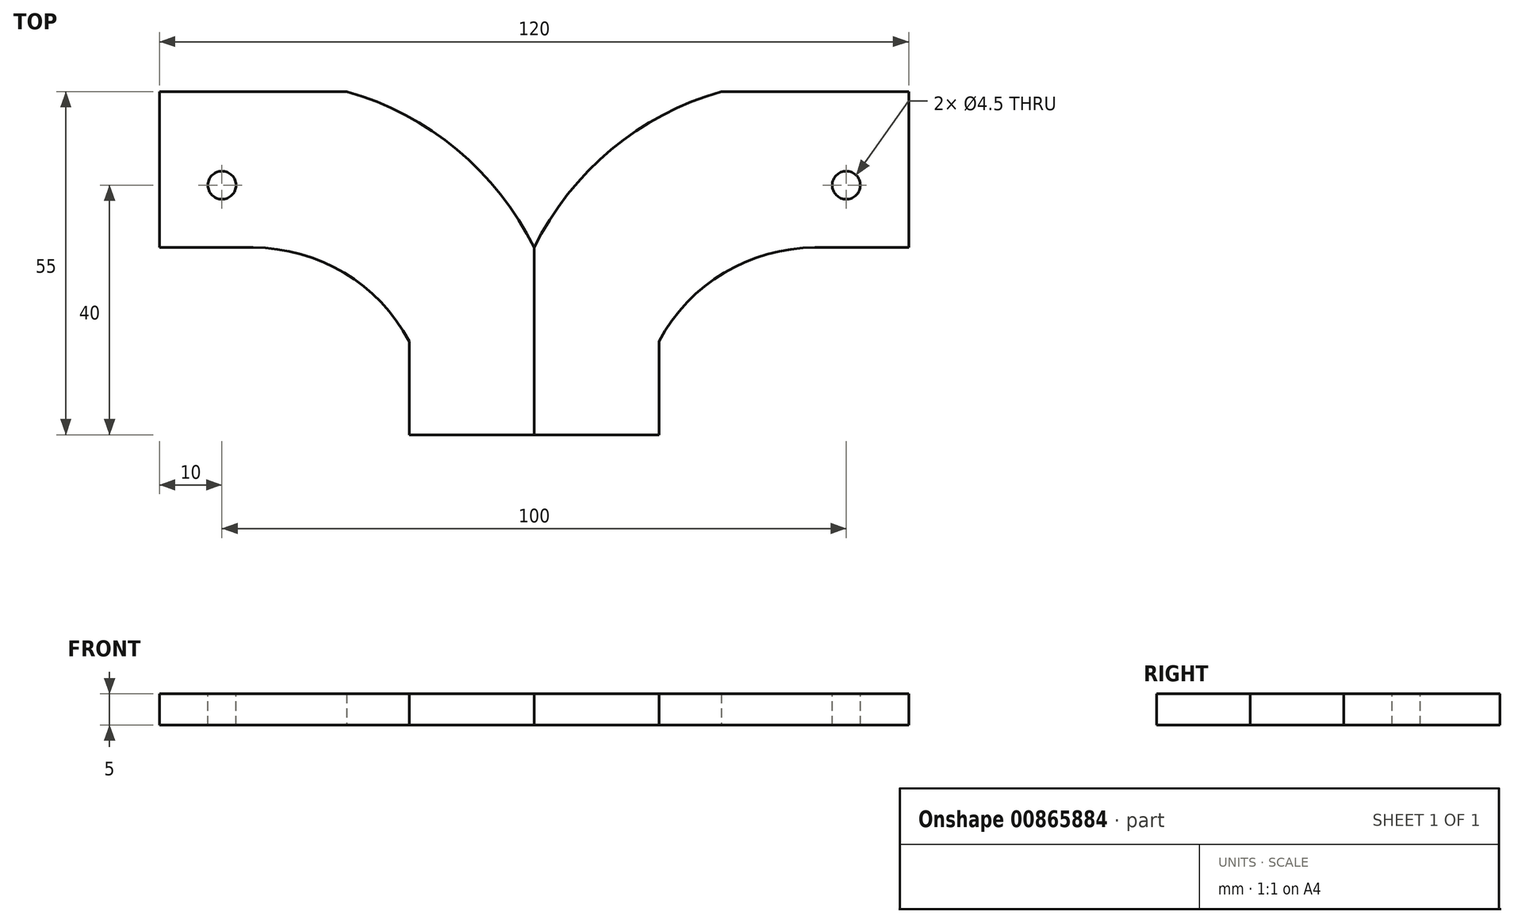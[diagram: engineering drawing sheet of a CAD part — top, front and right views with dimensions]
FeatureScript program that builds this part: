
annotation { "Feature Type Name" : "Feature", "Feature Type Description" : "" }
export const myFeature = defineFeature(function(context is Context, id is Id, definition is map)
    precondition{}
    {
        {
            var Q0;
            Q0=qCreatedBy(makeId("Top.planeOp"),FACE);
            var sketch = newSketch(context, id + "F0", { "sketchPlane" : qUnion([Q0])});
            skLineSegment(sketch, "E0", {"start": v(0, 0) * mm, "end": v(-20, 0) * mm});
            skLineSegment(sketch, "E1", {"start": v(-20, 0) * mm, "end": v(-20, 15) * mm});
            skLineSegment(sketch, "E2", {"start": v(-45, 30) * mm, "end": v(-60, 30) * mm});
            skLineSegment(sketch, "E3", {"start": v(-60, 30) * mm, "end": v(-60, 55) * mm});
            skLineSegment(sketch, "E4", {"start": v(-60, 55) * mm, "end": v(-30, 55) * mm});
            skLineSegment(sketch, "E5", {"start": v(0, 30) * mm, "end": v(0, 0) * mm});
            skArc(sketch, "E6", {"start": v(-20, 15) * mm, "mid": v(-30.42, 25.96) * mm, "end": v(-45, 30) * mm});
            skArc(sketch, "E7", {"start": v(0, 30) * mm, "mid": v(-12.34, 45.69) * mm, "end": v(-30, 55) * mm});
            skSolve(sketch);
        }
        {
            var Q0;
            Q0 = qSketchRegion(id + "F0", true);
            extrude(context, id + "F1", {"entities" : qUnion([Q0]), "depth" : 5 * mm, "offsetDistance" : 25 * mm});
        }
        {
            var Q0;
            Q0=makeQuery(id+"F1.opExtrude","CAP_FACE",FACE,{"disambiguationData":[OSD([sQuery(id+"F0.wireOp",EDGE,"E0"),sQuery(id+"F0.wireOp",EDGE,"E1"),sQuery(id+"F0.wireOp",EDGE,"E2"),sQuery(id+"F0.wireOp",EDGE,"E3"),sQuery(id+"F0.wireOp",EDGE,"E4"),sQuery(id+"F0.wireOp",EDGE,"E5"),sQuery(id+"F0.wireOp",EDGE,"E6"),sQuery(id+"F0.wireOp",EDGE,"E7")])],"isStart":false});
            var sketch = newSketch(context, id + "F2", { "sketchPlane" : qUnion([Q0])});
            skCircle(sketch, "E8", {"center": v(-50, 40) * mm, "radius": 2.25 * mm});
            skSolve(sketch);
        }
        {
            var Q0;
            Q0 = qSketchRegion(id + "F2", true);
            extrude(context, id + "F3", {"entities" : qUnion([Q0]), "operationType" : NewBodyOperationType.REMOVE, "endBound" : BoundingType.THROUGH_ALL, "oppositeDirection" : true, "depth" : 25 * mm, "offsetDistance" : 25 * mm});
        }
        {
            var Q0;
            Q0=makeQuery(id+"F1.opExtrude","SWEPT_BODY",BODY,{"disambiguationData":[OSD([sQuery(id+"F0.wireOp",EDGE,"E0"),sQuery(id+"F0.wireOp",EDGE,"E1"),sQuery(id+"F0.wireOp",EDGE,"E2"),sQuery(id+"F0.wireOp",EDGE,"E3"),sQuery(id+"F0.wireOp",EDGE,"E4"),sQuery(id+"F0.wireOp",EDGE,"E5"),sQuery(id+"F0.wireOp",EDGE,"E6"),sQuery(id+"F0.wireOp",EDGE,"E7")])]});
            var Q1;
            Q1=qCreatedBy(makeId("Right.planeOp"),FACE);
            mirror(context, id + "F4", {"entities" : qUnion([Q0]), "mirrorPlane" : qUnion([Q1])});
        }
    });
